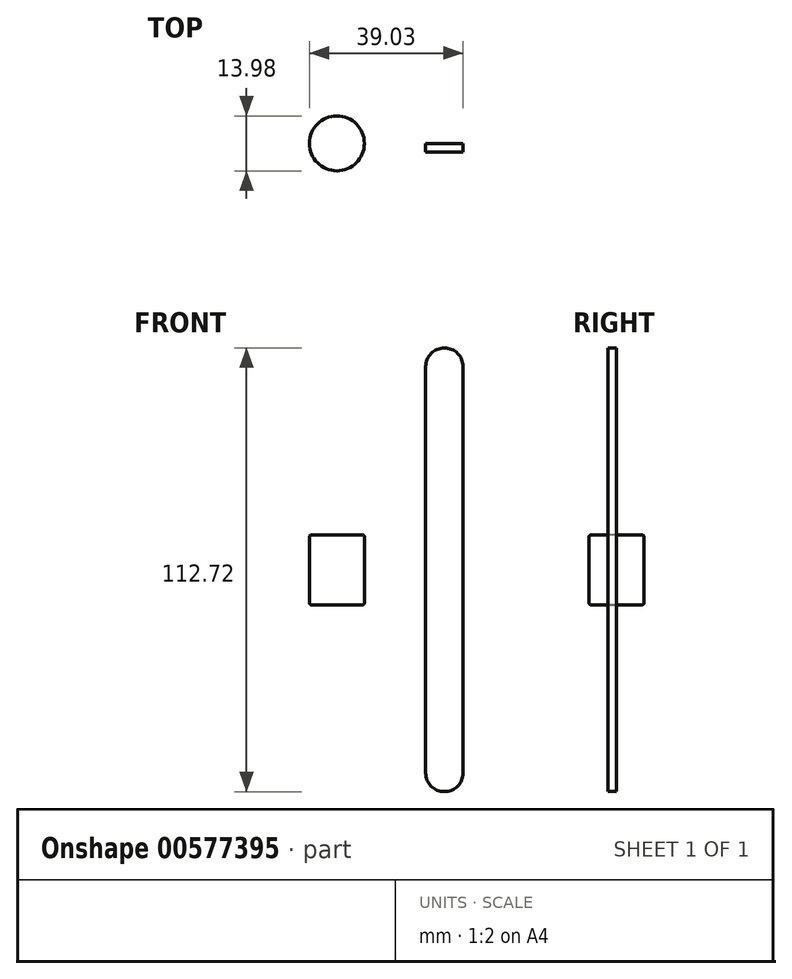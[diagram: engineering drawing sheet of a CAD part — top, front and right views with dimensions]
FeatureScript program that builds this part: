
annotation { "Feature Type Name" : "Feature", "Feature Type Description" : "" }
export const myFeature = defineFeature(function(context is Context, id is Id, definition is map)
    precondition{}
    {
        {
            var Q0;
            Q0=qCreatedBy(makeId("Front.planeOp"),FACE);
            var sketch = newSketch(context, id + "F0", { "sketchPlane" : qUnion([Q0])});
            skLineSegment(sketch, "E0", {"start": v(-58.53, 11.43) * mm, "end": v(-58.53, -11.43) * mm, "construction": true});
            skPoint(sketch, "E1", {"position": v(-58.53, 0) * mm});
            skPoint(sketch, "E2", {"position": v(0, 0) * mm});
            skLineSegment(sketch, "E3", {"start": v(-58.53, 8.89) * mm, "end": v(-51.55, 8.89) * mm});
            skLineSegment(sketch, "E4", {"start": v(-51.55, 8.89) * mm, "end": v(-51.55, -8.89) * mm});
            skLineSegment(sketch, "E5", {"start": v(-51.55, -8.89) * mm, "end": v(-58.53, -8.89) * mm});
            skPoint(sketch, "E6", {"position": v(-51.55, 0) * mm});
            skLineSegment(sketch, "E7", {"start": v(-58.53, 8.89) * mm, "end": v(-58.53, -8.89) * mm});
            skSolve(sketch);
        }
        {
            var Q0;
            Q0 = qSketchRegion(id + "F0", true);
            var Q1;
            Q1=sQuery(id+"F0.wireOp",EDGE,"E0");
            revolve(context, id + "F1", {"entities" : qUnion([Q0]), "axis" : qUnion([Q1]), "revolveType" : RevolveType.FULL});
        }
        {
            var Q0;
            Q0=makeQuery(id+"F1.opRevolve","SWEPT_EDGE",EDGE,{"disambiguationData":[OSD([sQuery(id+"F0.wireOp",EDGE,"E3"),sQuery(id+"F0.wireOp",EDGE,"E4")])]});
            var Q1;
            Q1=makeQuery(id+"F1.opRevolve","SWEPT_FACE",FACE,{"disambiguationData":[OSD([sQuery(id+"F0.wireOp",EDGE,"E4")])]});
            fillet(context, id + "F2", {"entities" : qUnion([Q0, Q1]), "radius" : 0.5 * mm, "tangentPropagation" : true, "allowEdgeOverflow" : false});
        }
        {
            var Q0;
            Q0=qCreatedBy(makeId("Front.planeOp"),FACE);
            var sketch = newSketch(context, id + "F3", { "sketchPlane" : qUnion([Q0])});
            skLineSegment(sketch, "E8", {"start": v(-26.49, 51.62) * mm, "end": v(-26.49, -51.62) * mm});
            skPoint(sketch, "E9", {"position": v(-26.49, 0) * mm});
            skLineSegment(sketch, "E10.0", {"start": v(-35.96, 51.62) * mm, "end": v(-35.96, -51.62) * mm});
            skArc(sketch, "E11", {"start": v(-26.49, 51.62) * mm, "mid": v(-31.23, 56.36) * mm, "end": v(-35.96, 51.62) * mm});
            skArc(sketch, "E12", {"start": v(-35.96, -51.62) * mm, "mid": v(-31.23, -56.36) * mm, "end": v(-26.49, -51.62) * mm});
            skLineSegment(sketch, "E13", {"start": v(-12.26, 56.36) * mm, "end": v(-50.65, 56.36) * mm, "construction": true});
            skLineSegment(sketch, "E14", {"start": v(-50.65, 56.36) * mm, "end": v(-50.65, -56.36) * mm, "construction": true});
            skLineSegment(sketch, "E15", {"start": v(-50.65, -56.36) * mm, "end": v(-7.58, -56.36) * mm, "construction": true});
            skSolve(sketch);
        }
        {
            var Q0;
            Q0 = qSketchRegion(id + "F3", true);
            extrude(context, id + "F4", {"entities" : qUnion([Q0]), "depth" : 2.16 * mm, "offsetDistance" : 25.4 * mm});
        }
    });
